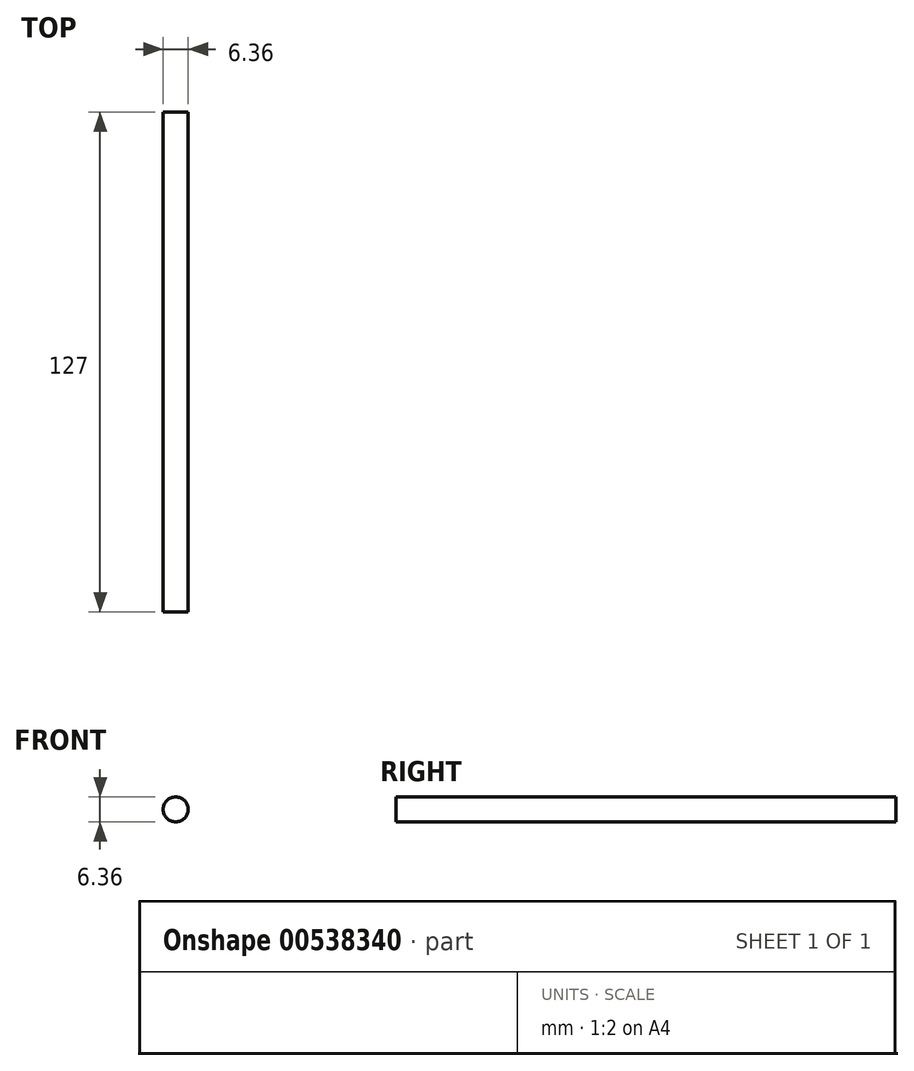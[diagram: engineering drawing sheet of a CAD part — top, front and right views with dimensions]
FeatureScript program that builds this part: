
annotation { "Feature Type Name" : "Feature", "Feature Type Description" : "" }
export const myFeature = defineFeature(function(context is Context, id is Id, definition is map)
    precondition{}
    {
        {
            var Q0;
            Q0=qCreatedBy(makeId("Front.planeOp"),FACE);
            var sketch = newSketch(context, id + "F0", { "sketchPlane" : qUnion([Q0])});
            skCircle(sketch, "E0", {"center": v(0, 0) * mm, "radius": 3.18 * mm});
            skSolve(sketch);
        }
        {
            var Q0;
            Q0 = qSketchRegion(id + "F0", true);
            extrude(context, id + "F1", {"entities" : qUnion([Q0]), "endBound" : BoundingType.SYMMETRIC, "depth" : 127 * mm, "offsetDistance" : 25.4 * mm});
        }
    });
